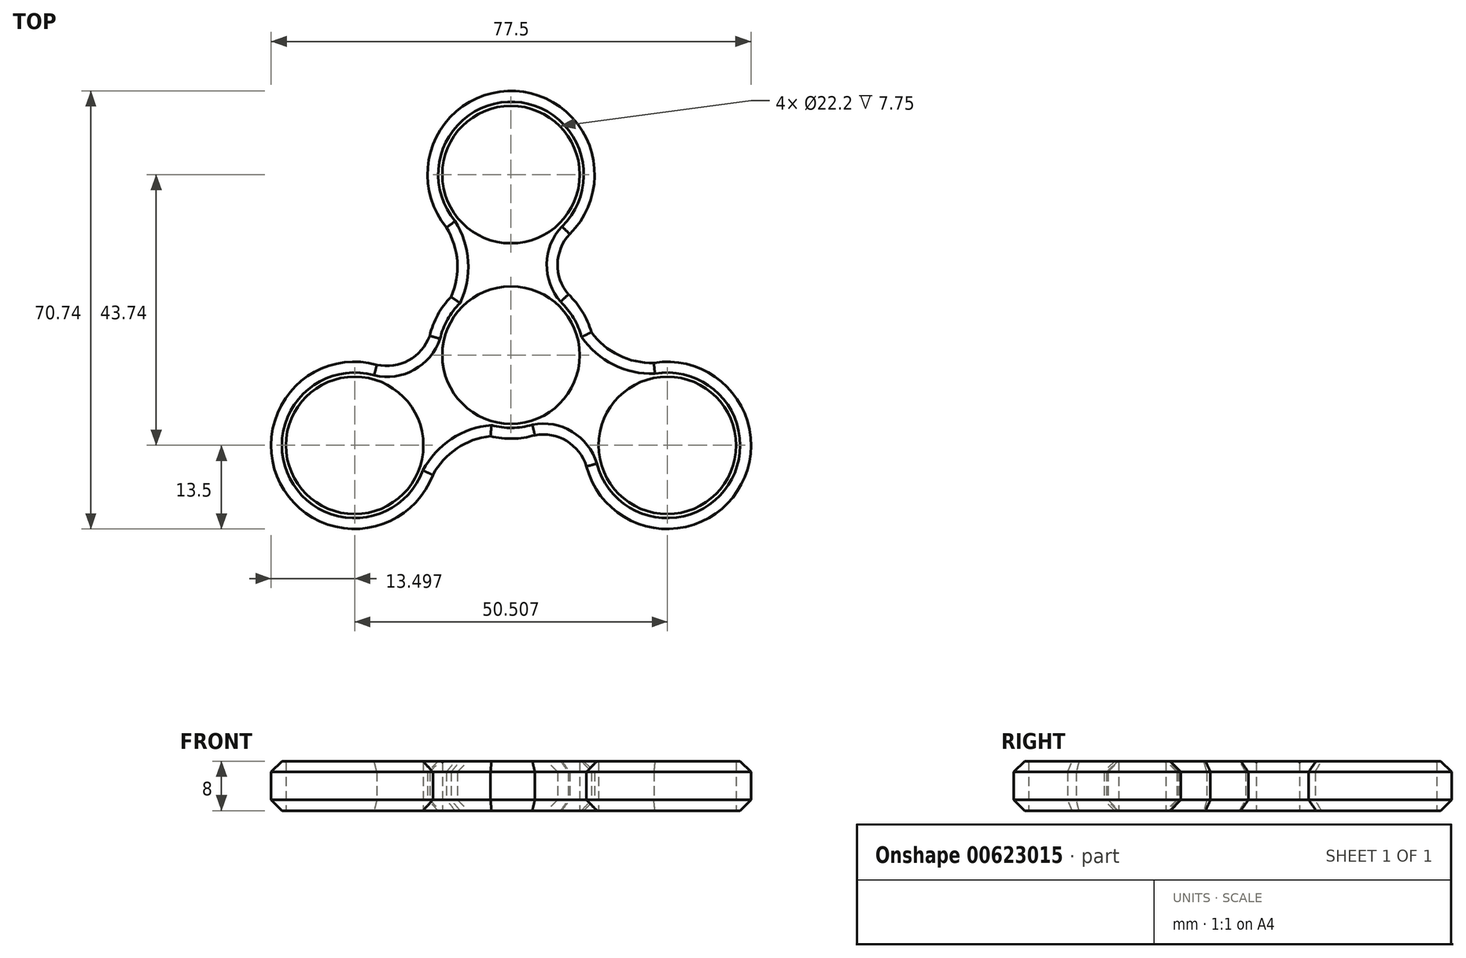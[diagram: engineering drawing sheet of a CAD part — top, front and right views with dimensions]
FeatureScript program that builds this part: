
annotation { "Feature Type Name" : "Feature", "Feature Type Description" : "" }
export const myFeature = defineFeature(function(context is Context, id is Id, definition is map)
    precondition{}
    {
        {
            var Q0;
            Q0=qCreatedBy(makeId("Top.planeOp"),FACE);
            var sketch = newSketch(context, id + "F0", { "sketchPlane" : qUnion([Q0])});
            skCircle(sketch, "E0", {"center": v(0, 0) * mm, "radius": 11.1 * mm});
            skCircle(sketch, "E1", {"center": v(0, 0) * mm, "radius": 13.5 * mm});
            skCircle(sketch, "E2", {"center": v(0, 29.16) * mm, "radius": 11.1 * mm});
            skCircle(sketch, "E3", {"center": v(0, 29.16) * mm, "radius": 13.5 * mm});
            skArc(sketch, "E4", {"start": v(-9.69, 9.4) * mm, "mid": v(-8.68, 15.1) * mm, "end": v(-10.44, 20.6) * mm});
            skArc(sketch, "E5", {"start": v(9.76, 19.84) * mm, "mid": v(7.53, 14.92) * mm, "end": v(9.27, 9.81) * mm});
            skCircle(sketch, "E6.1.0", {"center": v(-25.25, -14.58) * mm, "radius": 13.5 * mm});
            skCircle(sketch, "E6.1.1", {"center": v(-25.25, -14.58) * mm, "radius": 11.1 * mm});
            skArc(sketch, "E6.1.2", {"start": v(-3.3, -13.1) * mm, "mid": v(-8.73, -15.07) * mm, "end": v(-12.62, -19.35) * mm});
            skArc(sketch, "E6.1.3", {"start": v(-22.06, -1.46) * mm, "mid": v(-16.69, -0.94) * mm, "end": v(-13.13, 3.13) * mm});
            skCircle(sketch, "E6.2.0", {"center": v(25.25, -14.58) * mm, "radius": 13.5 * mm});
            skCircle(sketch, "E6.2.1", {"center": v(25.25, -14.58) * mm, "radius": 11.1 * mm});
            skArc(sketch, "E6.2.2", {"start": v(12.99, 3.7) * mm, "mid": v(17.41, -0.03) * mm, "end": v(23.07, -1.26) * mm});
            skArc(sketch, "E6.2.3", {"start": v(12.3, -18.37) * mm, "mid": v(9.16, -13.98) * mm, "end": v(3.86, -12.94) * mm});
            skSolve(sketch);
        }
        {
            var Q0;
            Q0=qSketchRegion(id+"F0",true);
            extrude(context, id + "F1", {"entities" : qUnion([Q0]), "depth" : 8 * mm});
        }
        {
            var Q0;
            Q0=makeQuery(id+"F1.opExtrude","CAP_EDGE",EDGE,{"disambiguationData":[OSD([sQuery(id+"F0.wireOp",EDGE,"E2")])],"isStart":false});
            var Q1;
            Q1=makeQuery(id+"F1.opExtrude","CAP_EDGE",EDGE,{"disambiguationData":[OSD([sQuery(id+"F0.wireOp",EDGE,"E6.1.1")])],"isStart":false});
            var Q2;
            Q2=makeQuery(id+"F1.opExtrude","CAP_EDGE",EDGE,{"disambiguationData":[OSD([sQuery(id+"F0.wireOp",EDGE,"E6.2.1")])],"isStart":false});
            var Q3;
            Q3=makeQuery(id+"F1.opExtrude","CAP_EDGE",EDGE,{"disambiguationData":[OSD([sQuery(id+"F0.wireOp",EDGE,"E0")])],"isStart":false});
            fillet(context, id + "F2", {"entities" : qUnion([Q0, Q1, Q2, Q3]), "radius" : 0.25 * mm, "tangentPropagation" : true, "allowEdgeOverflow" : false});
        }
        {
            var Q0;
            Q0=makeQuery(id+"F1.opExtrude","CAP_EDGE",EDGE,{"disambiguationData":[OSD([sQuery(id+"F0.wireOp",EDGE,"E6.1.0")])],"isStart":true});
            var Q1;
            Q1=makeQuery(id+"F1.opExtrude","CAP_EDGE",EDGE,{"disambiguationData":[OSD([sQuery(id+"F0.wireOp",EDGE,"E6.1.3")])],"isStart":true});
            var Q2;
            Q2=makeQuery(id+"F1.opExtrude","CAP_EDGE",EDGE,{"disambiguationData":[OSD([sQuery(id+"F0.wireOp",EDGE,"E6.1.2")])],"isStart":true});
            var Q3;
            {var subQ0=sQuery(id+"F0.wireOp",EDGE,"E1");Q3=makeQuery(id+"F1.opExtrude","CAP_EDGE",EDGE,{"disambiguationData":[OSD([subQ0]),TDD([makeQuery(id+"F0.imprint","IMPRINT",EDGE,{"disambiguationData":[TD([[makeQuery(id+"F0.imprint","INTERSECT",VERTEX,{"derivedFrom":[subQ0,sQuery(id+"F0.wireOp",EDGE,"E6.1.2")]}),-1.0]])],"derivedFrom":subQ0})])],"isStart":true});}
            var Q4;
            Q4=makeQuery(id+"F1.opExtrude","CAP_EDGE",EDGE,{"disambiguationData":[OSD([sQuery(id+"F0.wireOp",EDGE,"E6.2.3")])],"isStart":true});
            var Q5;
            Q5=makeQuery(id+"F1.opExtrude","CAP_EDGE",EDGE,{"disambiguationData":[OSD([sQuery(id+"F0.wireOp",EDGE,"E6.2.0")])],"isStart":true});
            var Q6;
            Q6=makeQuery(id+"F1.opExtrude","CAP_EDGE",EDGE,{"disambiguationData":[OSD([sQuery(id+"F0.wireOp",EDGE,"E6.2.2")])],"isStart":true});
            var Q7;
            {var subQ0=sQuery(id+"F0.wireOp",EDGE,"E1");Q7=makeQuery(id+"F1.opExtrude","CAP_EDGE",EDGE,{"disambiguationData":[OSD([subQ0]),TDD([makeQuery(id+"F0.imprint","IMPRINT",EDGE,{"disambiguationData":[TD([[makeQuery(id+"F0.imprint","INTERSECT",VERTEX,{"derivedFrom":[subQ0,sQuery(id+"F0.wireOp",EDGE,"E5")]}),1.0]])],"derivedFrom":subQ0})])],"isStart":true});}
            var Q8;
            Q8=makeQuery(id+"F1.opExtrude","CAP_EDGE",EDGE,{"disambiguationData":[OSD([sQuery(id+"F0.wireOp",EDGE,"E5")])],"isStart":true});
            var Q9;
            Q9=makeQuery(id+"F1.opExtrude","CAP_EDGE",EDGE,{"disambiguationData":[OSD([sQuery(id+"F0.wireOp",EDGE,"E3")])],"isStart":true});
            var Q10;
            Q10=makeQuery(id+"F1.opExtrude","CAP_EDGE",EDGE,{"disambiguationData":[OSD([sQuery(id+"F0.wireOp",EDGE,"E4")])],"isStart":true});
            var Q11;
            {var subQ0=sQuery(id+"F0.wireOp",EDGE,"E1");Q11=makeQuery(id+"F1.opExtrude","CAP_EDGE",EDGE,{"disambiguationData":[OSD([subQ0]),TDD([makeQuery(id+"F0.imprint","IMPRINT",EDGE,{"disambiguationData":[TD([[makeQuery(id+"F0.imprint","INTERSECT",VERTEX,{"derivedFrom":[subQ0,sQuery(id+"F0.wireOp",EDGE,"E4")]}),-1.0]])],"derivedFrom":subQ0})])],"isStart":true});}
            var Q12;
            Q12=makeQuery(id+"F1.opExtrude","CAP_EDGE",EDGE,{"disambiguationData":[OSD([sQuery(id+"F0.wireOp",EDGE,"E3")])],"isStart":false});
            var Q13;
            Q13=makeQuery(id+"F1.opExtrude","CAP_EDGE",EDGE,{"disambiguationData":[OSD([sQuery(id+"F0.wireOp",EDGE,"E5")])],"isStart":false});
            var Q14;
            {var subQ0=sQuery(id+"F0.wireOp",EDGE,"E1");Q14=makeQuery(id+"F1.opExtrude","CAP_EDGE",EDGE,{"disambiguationData":[OSD([subQ0]),TDD([makeQuery(id+"F0.imprint","IMPRINT",EDGE,{"disambiguationData":[TD([[makeQuery(id+"F0.imprint","INTERSECT",VERTEX,{"derivedFrom":[subQ0,sQuery(id+"F0.wireOp",EDGE,"E5")]}),1.0]])],"derivedFrom":subQ0})])],"isStart":false});}
            var Q15;
            Q15=makeQuery(id+"F1.opExtrude","CAP_EDGE",EDGE,{"disambiguationData":[OSD([sQuery(id+"F0.wireOp",EDGE,"E6.2.2")])],"isStart":false});
            var Q16;
            Q16=makeQuery(id+"F1.opExtrude","CAP_EDGE",EDGE,{"disambiguationData":[OSD([sQuery(id+"F0.wireOp",EDGE,"E6.2.0")])],"isStart":false});
            var Q17;
            Q17=makeQuery(id+"F1.opExtrude","CAP_EDGE",EDGE,{"disambiguationData":[OSD([sQuery(id+"F0.wireOp",EDGE,"E4")])],"isStart":false});
            var Q18;
            {var subQ0=sQuery(id+"F0.wireOp",EDGE,"E1");Q18=makeQuery(id+"F1.opExtrude","CAP_EDGE",EDGE,{"disambiguationData":[OSD([subQ0]),TDD([makeQuery(id+"F0.imprint","IMPRINT",EDGE,{"disambiguationData":[TD([[makeQuery(id+"F0.imprint","INTERSECT",VERTEX,{"derivedFrom":[subQ0,sQuery(id+"F0.wireOp",EDGE,"E4")]}),-1.0]])],"derivedFrom":subQ0})])],"isStart":false});}
            var Q19;
            Q19=makeQuery(id+"F1.opExtrude","CAP_EDGE",EDGE,{"disambiguationData":[OSD([sQuery(id+"F0.wireOp",EDGE,"E6.1.3")])],"isStart":false});
            var Q20;
            Q20=makeQuery(id+"F1.opExtrude","CAP_EDGE",EDGE,{"disambiguationData":[OSD([sQuery(id+"F0.wireOp",EDGE,"E6.1.0")])],"isStart":false});
            var Q21;
            Q21=makeQuery(id+"F1.opExtrude","CAP_EDGE",EDGE,{"disambiguationData":[OSD([sQuery(id+"F0.wireOp",EDGE,"E6.1.2")])],"isStart":false});
            var Q22;
            Q22=makeQuery(id+"F1.opExtrude","CAP_EDGE",EDGE,{"disambiguationData":[OSD([sQuery(id+"F0.wireOp",EDGE,"E6.2.3")])],"isStart":false});
            var Q23;
            {var subQ0=sQuery(id+"F0.wireOp",EDGE,"E1");Q23=makeQuery(id+"F1.opExtrude","CAP_EDGE",EDGE,{"disambiguationData":[OSD([subQ0]),TDD([makeQuery(id+"F0.imprint","IMPRINT",EDGE,{"disambiguationData":[TD([[makeQuery(id+"F0.imprint","INTERSECT",VERTEX,{"derivedFrom":[subQ0,sQuery(id+"F0.wireOp",EDGE,"E6.1.2")]}),-1.0]])],"derivedFrom":subQ0})])],"isStart":false});}
            chamfer(context, id + "F3", {"entities" : qUnion([Q0, Q1, Q2, Q3, Q4, Q5, Q6, Q7, Q8, Q9, Q10, Q11, Q12, Q13, Q14, Q15, Q16, Q17, Q18, Q19, Q20, Q21, Q22, Q23]), "chamferType" : ChamferType.OFFSET_ANGLE, "width" : 1.75 * mm, "oppositeDirection" : false, "angle" : 45 * degree, "tangentPropagation" : true});
        }
    });
